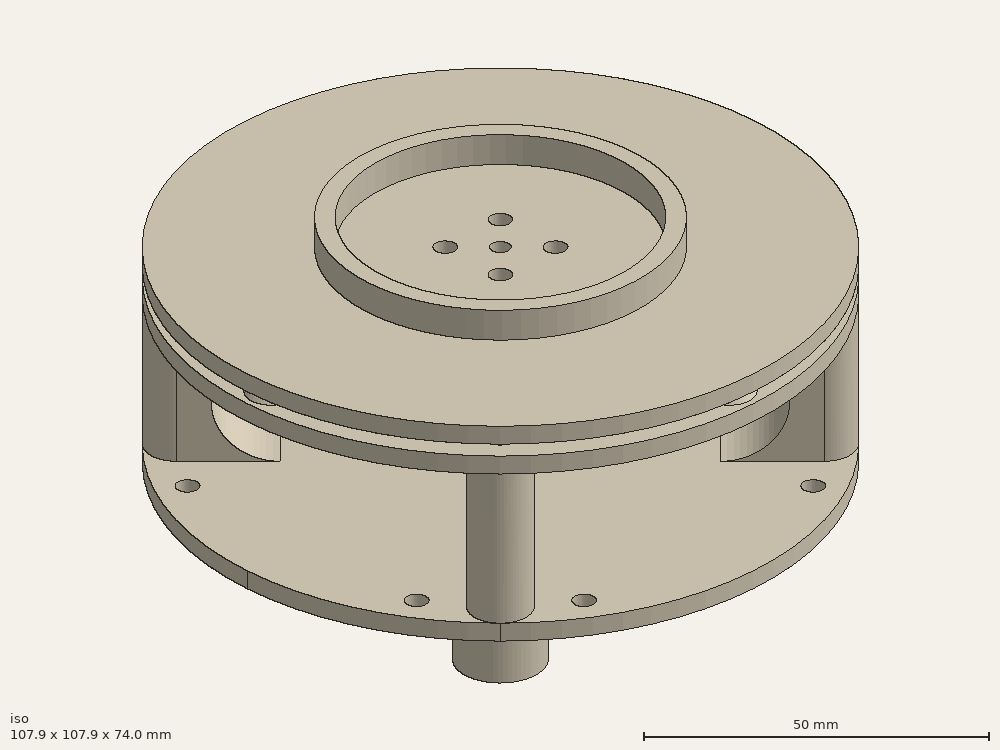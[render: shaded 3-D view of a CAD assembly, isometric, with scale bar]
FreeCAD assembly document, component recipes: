
FREECAD ASSEMBLY — COMPONENT RECIPES ("horiz")

This assembly document has 7 components, labeled P0..P6 below (a component is one placed body or linked part). 7 of them carry a construction recipe — the FreeCAD feature program that regenerates the part from scratch, quoted from this document or its linked companion documents; the rest are supplied as boundary geometry only. No exploded tour is included for this assembly.
COMPONENT P0 — recipe-attached ("Wheel", modeled in this document).
Construction recipe (the document's own serialized feature program — sketch geometry with constraints, then the solid features built on it; lengths are millimeters unless a unit is written):

FEATURE [Sketcher::SketchObject] Sketch001
  ArcFitTolerance = 1e-06
  AttachmentSupport = -> [XY_Plane]
  FullyConstrained = true
  MakeInternals = false
  MapMode = 5
  sketch-geometry (2):
    g0: Circle CenterX=0 CenterY=0 CenterZ=0 NormalX=0 NormalY=0 NormalZ=1 AngleXU=0 Radius=52
    g1: Circle CenterX=0 CenterY=0 CenterZ=0 NormalX=0 NormalY=0 NormalZ=1 AngleXU=0 Radius=1.6
  constraints (4):
    c: Coincident(g0,g-1)
    c: Radius(g0) = 52
    c: Coincident(g1,g0)
    c: Radius(g1) = 1.6
FEATURE [PartDesign::Pad] Pad001
  Direction = (0,0,1)
  Length = 3
  Length2 = 10
  Profile = -> Sketch001
  ReferenceAxis = -> Sketch001 [N_Axis]
  Reversed = true
  Suppressed = false
  Type = 0
FEATURE [Sketcher::SketchObject] Sketch
  ArcFitTolerance = 1e-06
  AttachmentSupport = -> [XY_Plane]
  FullyConstrained = true
  MakeInternals = false
  MapMode = 5
  sketch-geometry (2):
    g0: Circle CenterX=0 CenterY=0 CenterZ=0 NormalX=0 NormalY=0 NormalZ=1 AngleXU=0 Radius=24
    g1: Circle CenterX=0 CenterY=0 CenterZ=0 NormalX=0 NormalY=0 NormalZ=1 AngleXU=0 Radius=27
  constraints (4):
    c: Coincident(g0,g-1)
    c: Coincident(g1,g0)
    c: Radius(g1) = 27
    c: Radius(g0) = 24
FEATURE [PartDesign::Pad] Pad
  BaseFeature = -> Pad001
  Direction = (0,0,1)
  Length = 5
  Length2 = 10
  Profile = -> Sketch
  ReferenceAxis = -> Sketch [N_Axis]
  Suppressed = false
  Type = 0
FEATURE [Sketcher::SketchObject] Sketch002
  ArcFitTolerance = 1e-06
  AttachmentSupport = -> [XY_Plane]
  FullyConstrained = true
  MakeInternals = false
  MapMode = 5
  sketch-geometry (9):
    g0: LineSegment [constr] StartX=-5.65685 StartY=5.65685 StartZ=0 EndX=-5.65685 EndY=-5.65685 EndZ=0
    g1: LineSegment [constr] StartX=-5.65685 StartY=-5.65685 StartZ=0 EndX=5.65685 EndY=-5.65685 EndZ=0
    g2: LineSegment [constr] StartX=5.65685 StartY=-5.65685 StartZ=0 EndX=5.65685 EndY=5.65685 EndZ=0
    g3: LineSegment [constr] StartX=5.65685 StartY=5.65685 StartZ=0 EndX=-5.65685 EndY=5.65685 EndZ=0
    g4: Circle [constr] CenterX=0 CenterY=0 CenterZ=0 NormalX=0 NormalY=0 NormalZ=1 AngleXU=0 Radius=8
    g5: Circle CenterX=5.65685 CenterY=5.65685 CenterZ=0 NormalX=0 NormalY=0 NormalZ=1 AngleXU=0 Radius=1.8
    g6: Circle CenterX=-5.65685 CenterY=5.65685 CenterZ=0 NormalX=0 NormalY=0 NormalZ=1 AngleXU=0 Radius=1.8
    g7: Circle CenterX=-5.65685 CenterY=-5.65685 CenterZ=0 NormalX=0 NormalY=0 NormalZ=1 AngleXU=0 Radius=1.8
    g8: Circle CenterX=5.65685 CenterY=-5.65685 CenterZ=0 NormalX=0 NormalY=0 NormalZ=1 AngleXU=0 Radius=1.8
  constraints (22):
    c: Coincident(g0,g1)
    c: Coincident(g1,g2)
    c: Coincident(g2,g3)
    c: Coincident(g3,g0)
    c: Equal(g0,g1)
    c: Equal(g0,g2)
    c: Equal(g0,g3)
    c: PointOnObject(g0,g4)
    c: PointOnObject(g1,g4)
    c: PointOnObject(g2,g4)
    c: PointOnObject(g3,g4)
    c: Coincident(g4,g-1)
    c: Radius(g4) = 8
    c: Parallel(g3,g-1)
    c: Coincident(g5,g2)
    c: Coincident(g6,g0)
    c: Coincident(g7,g0)
    c: Coincident(g8,g1)
    c: Equal(g8,g5)
    c: Equal(g5,g6)
    c: Equal(g6,g7)
    c: Radius(g5) = 1.8
FEATURE [PartDesign::Pocket] Pocket
  BaseFeature = -> Pad
  Direction = (0,0,-1)
  Length = 5
  Length2 = 5
  Profile = -> Sketch002
  ReferenceAxis = -> Sketch002 [N_Axis]
  Suppressed = false
  Type = 0
FEATURE [PartDesign::Body] Body  label="Wheel"
  AllowCompound = false
  Group = -> [Pad001,Sketch001,Sketch,Pad,Sketch002,Pocket]
  Origin = -> Origin
  Placement = pos=(-1.14e-14,-1.2e-14,59) rot=(0,0,-1;3.14159rad)
  Tip = -> Pocket
COMPONENT P1 — recipe-attached ("Mid", modeled in this document).
Construction recipe (the document's own serialized feature program — sketch geometry with constraints, then the solid features built on it; lengths are millimeters unless a unit is written):

FEATURE [Sketcher::SketchObject] Sketch003
  ArcFitTolerance = 1e-06
  AttachmentSupport = -> [XY_Plane001]
  FullyConstrained = true
  MakeInternals = false
  MapMode = 5
  sketch-geometry (11):
    g0: Circle CenterX=0 CenterY=0 CenterZ=0 NormalX=0 NormalY=0 NormalZ=1 AngleXU=0 Radius=52
    g1: Circle CenterX=0 CenterY=0 CenterZ=0 NormalX=0 NormalY=0 NormalZ=1 AngleXU=0 Radius=1.6
    g2: LineSegment [constr] StartX=-8.48528 StartY=8.48528 StartZ=0 EndX=-8.48528 EndY=-8.48528 EndZ=0
    g3: LineSegment [constr] StartX=-8.48528 StartY=-8.48528 StartZ=0 EndX=8.48528 EndY=-8.48528 EndZ=0
    g4: LineSegment [constr] StartX=8.48528 StartY=-8.48528 StartZ=0 EndX=8.48528 EndY=8.48528 EndZ=0
    g5: LineSegment [constr] StartX=8.48528 StartY=8.48528 StartZ=0 EndX=-8.48528 EndY=8.48528 EndZ=0
    g6: Circle [constr] CenterX=0 CenterY=0 CenterZ=0 NormalX=0 NormalY=0 NormalZ=1 AngleXU=0 Radius=12
    g7: Circle CenterX=8.48528 CenterY=8.48528 CenterZ=0 NormalX=0 NormalY=0 NormalZ=1 AngleXU=0 Radius=2.2
    g8: Circle CenterX=-8.48528 CenterY=8.48528 CenterZ=0 NormalX=0 NormalY=0 NormalZ=1 AngleXU=0 Radius=2.2
    g9: Circle CenterX=-8.48528 CenterY=-8.48528 CenterZ=0 NormalX=0 NormalY=0 NormalZ=1 AngleXU=0 Radius=2.2
    g10: Circle CenterX=8.48528 CenterY=-8.48528 CenterZ=0 NormalX=0 NormalY=0 NormalZ=1 AngleXU=0 Radius=2.2
  constraints (26):
    c: Coincident(g0,g-1)
    c: Radius(g0) = 52
    c: Coincident(g1,g0)
    c: Radius(g1) = 1.6
    c: Coincident(g2,g3)
    c: Coincident(g3,g4)
    c: Coincident(g4,g5)
    c: Coincident(g5,g2)
    c: Equal(g2,g3)
    c: Equal(g2,g4)
    c: Equal(g2,g5)
    c: PointOnObject(g2,g6)
    c: PointOnObject(g3,g6)
    c: PointOnObject(g4,g6)
    c: PointOnObject(g5,g6)
    c: Coincident(g6,g0)
    c: Radius(g6) = 12
    c: Parallel(g5,g-1)
    c: Coincident(g7,g4)
    c: Coincident(g8,g2)
    c: Coincident(g9,g2)
    c: Coincident(g10,g3)
    c: Equal(g10,g7)
    c: Equal(g7,g8)
    c: Equal(g8,g9)
    c: Radius(g7) = 2.2
FEATURE [PartDesign::Pad] Pad002
  Direction = (0,0,1)
  Length = 3
  Length2 = 10
  Profile = -> Sketch003
  ReferenceAxis = -> Sketch003 [N_Axis]
  Suppressed = false
  Type = 0
FEATURE [Sketcher::SketchObject] Sketch005
  ArcFitTolerance = 1e-06
  AttachmentSupport = -> [XY_Plane001]
  FullyConstrained = true
  MakeInternals = false
  MapMode = 5
  sketch-geometry (9):
    g0: LineSegment [constr] StartX=33.234 StartY=33.234 StartZ=0 EndX=-33.234 EndY=33.234 EndZ=0
    g1: LineSegment [constr] StartX=-33.234 StartY=33.234 StartZ=0 EndX=-33.234 EndY=-33.234 EndZ=0
    g2: LineSegment [constr] StartX=-33.234 StartY=-33.234 StartZ=0 EndX=33.234 EndY=-33.234 EndZ=0
    g3: LineSegment [constr] StartX=33.234 StartY=-33.234 StartZ=0 EndX=33.234 EndY=33.234 EndZ=0
    g4: Circle [constr] CenterX=-2e-16 CenterY=0 CenterZ=0 NormalX=0 NormalY=0 NormalZ=1 AngleXU=0 Radius=47
    g5: Circle CenterX=33.234 CenterY=33.234 CenterZ=0 NormalX=0 NormalY=0 NormalZ=1 AngleXU=0 Radius=5
    g6: Circle CenterX=-33.234 CenterY=33.234 CenterZ=0 NormalX=0 NormalY=0 NormalZ=1 AngleXU=0 Radius=5
    g7: Circle CenterX=-33.234 CenterY=-33.234 CenterZ=0 NormalX=0 NormalY=0 NormalZ=1 AngleXU=0 Radius=5
    g8: Circle CenterX=33.234 CenterY=-33.234 CenterZ=0 NormalX=0 NormalY=0 NormalZ=1 AngleXU=0 Radius=5
  constraints (22):
    c: Coincident(g0,g1)
    c: Coincident(g1,g2)
    c: Coincident(g2,g3)
    c: Coincident(g3,g0)
    c: Equal(g0,g1)
    c: Equal(g0,g2)
    c: Equal(g0,g3)
    c: PointOnObject(g0,g4)
    c: PointOnObject(g1,g4)
    c: PointOnObject(g2,g4)
    c: PointOnObject(g3,g4)
    c: Coincident(g4,g-1)
    c: Radius(g4) = 47
    c: Parallel(g0,g-1)
    c: Coincident(g5,g0)
    c: Coincident(g6,g0)
    c: Coincident(g7,g1)
    c: Coincident(g8,g2)
    c: Equal(g8,g5)
    c: Equal(g5,g6)
    c: Equal(g6,g7)
    c: Radius(g6) = 5
FEATURE [PartDesign::Pad] Pad004
  BaseFeature = -> Pad002
  Direction = (0,0,1)
  Length = 28
  Length2 = 10
  Profile = -> Sketch005
  ReferenceAxis = -> Sketch005 [N_Axis]
  Suppressed = false
  Type = 0
FEATURE [Sketcher::SketchObject] Sketch007
  ArcFitTolerance = 1e-06
  AttachmentOffset = pos=(0,0,28) rot=(0,0,1;0rad)
  AttachmentSupport = -> [XY_Plane001]
  FullyConstrained = true
  MakeInternals = false
  MapMode = 5
  Placement = pos=(0,0,28) rot=(0,0,1;0rad)
  sketch-geometry (9):
    g0: LineSegment [constr] StartX=-33.234 StartY=33.234 StartZ=0 EndX=-33.234 EndY=-33.234 EndZ=0
    g1: LineSegment [constr] StartX=-33.234 StartY=-33.234 StartZ=0 EndX=33.234 EndY=-33.234 EndZ=0
    g2: LineSegment [constr] StartX=33.234 StartY=-33.234 StartZ=0 EndX=33.234 EndY=33.234 EndZ=0
    g3: LineSegment [constr] StartX=33.234 StartY=33.234 StartZ=0 EndX=-33.234 EndY=33.234 EndZ=0
    g4: Circle [constr] CenterX=0 CenterY=0 CenterZ=0 NormalX=0 NormalY=0 NormalZ=1 AngleXU=0 Radius=47
    g5: Circle CenterX=33.234 CenterY=33.234 CenterZ=0 NormalX=0 NormalY=0 NormalZ=1 AngleXU=0 Radius=1.5
    g6: Circle CenterX=-33.234 CenterY=33.234 CenterZ=0 NormalX=0 NormalY=0 NormalZ=1 AngleXU=0 Radius=1.5
    g7: Circle CenterX=-33.234 CenterY=-33.234 CenterZ=0 NormalX=0 NormalY=0 NormalZ=1 AngleXU=0 Radius=1.5
    g8: Circle CenterX=33.234 CenterY=-33.234 CenterZ=0 NormalX=0 NormalY=0 NormalZ=1 AngleXU=0 Radius=1.5
  constraints (22):
    c: Coincident(g0,g1)
    c: Coincident(g1,g2)
    c: Coincident(g2,g3)
    c: Coincident(g3,g0)
    c: Equal(g0,g1)
    c: Equal(g0,g2)
    c: Equal(g0,g3)
    c: PointOnObject(g0,g4)
    c: PointOnObject(g1,g4)
    c: PointOnObject(g2,g4)
    c: PointOnObject(g3,g4)
    c: Coincident(g4,g-1)
    c: Radius(g4) = 47
    c: Parallel(g3,g-1)
    c: Coincident(g5,g2)
    c: Coincident(g6,g0)
    c: Coincident(g7,g0)
    c: Coincident(g8,g1)
    c: Equal(g8,g5)
    c: Equal(g5,g6)
    c: Equal(g6,g7)
    c: Radius(g6) = 1.5
FEATURE [PartDesign::Pocket] Pocket002
  BaseFeature = -> Pad004
  Direction = (0,0,-1)
  Length = 10
  Length2 = 5
  Profile = -> Sketch007
  ReferenceAxis = -> Sketch007 [N_Axis]
  Suppressed = false
  Type = 0
FEATURE [Sketcher::SketchObject] Sketch011
  ArcFitTolerance = 1e-06
  AttachmentSupport = -> [XY_Plane001]
  FullyConstrained = true
  MakeInternals = false
  MapMode = 5
  sketch-geometry (17):
    g0: LineSegment [constr] StartX=-23.5 StartY=-40.7032 StartZ=0 EndX=40.7032 EndY=-23.5 EndZ=0
    g1: LineSegment [constr] StartX=40.7032 StartY=-23.5 StartZ=0 EndX=23.5 EndY=40.7032 EndZ=0
    g2: LineSegment [constr] StartX=23.5 StartY=40.7032 StartZ=0 EndX=-40.7032 EndY=23.5 EndZ=0
    g3: LineSegment [constr] StartX=-40.7032 StartY=23.5 StartZ=0 EndX=-23.5 EndY=-40.7032 EndZ=0
    g4: Circle [constr] CenterX=0 CenterY=0 CenterZ=0 NormalX=0 NormalY=0 NormalZ=1 AngleXU=0 Radius=47
    g5: Circle CenterX=23.5 CenterY=40.7032 CenterZ=0 NormalX=0 NormalY=0 NormalZ=1 AngleXU=0 Radius=1.8
    g6: Circle CenterX=-40.7032 CenterY=23.5 CenterZ=0 NormalX=0 NormalY=0 NormalZ=1 AngleXU=0 Radius=1.8
    g7: Circle CenterX=-23.5 CenterY=-40.7032 CenterZ=0 NormalX=0 NormalY=0 NormalZ=1 AngleXU=0 Radius=1.8
    g8: Circle CenterX=40.7032 CenterY=-23.5 CenterZ=0 NormalX=0 NormalY=0 NormalZ=1 AngleXU=0 Radius=1.8
    g9: LineSegment [constr] StartX=-23.5 StartY=40.7032 StartZ=0 EndX=40.7032 EndY=23.5 EndZ=0
    g10: LineSegment [constr] StartX=40.7032 StartY=23.5 StartZ=0 EndX=23.5 EndY=-40.7032 EndZ=0
    g11: LineSegment [constr] StartX=23.5 StartY=-40.7032 StartZ=0 EndX=-40.7032 EndY=-23.5 EndZ=0
    g12: LineSegment [constr] StartX=-40.7032 StartY=-23.5 StartZ=0 EndX=-23.5 EndY=40.7032 EndZ=0
    g13: Circle CenterX=-23.5 CenterY=40.7032 CenterZ=0 NormalX=0 NormalY=0 NormalZ=1 AngleXU=0 Radius=1.8
    g14: Circle CenterX=40.7032 CenterY=23.5 CenterZ=0 NormalX=0 NormalY=0 NormalZ=1 AngleXU=0 Radius=1.8
    g15: Circle CenterX=23.5 CenterY=-40.7032 CenterZ=0 NormalX=0 NormalY=0 NormalZ=1 AngleXU=0 Radius=1.8
    g16: Circle CenterX=-40.7032 CenterY=-23.5 CenterZ=0 NormalX=0 NormalY=0 NormalZ=1 AngleXU=0 Radius=1.8
  constraints (42):
    c: Coincident(g0,g1)
    c: Coincident(g1,g2)
    c: Coincident(g2,g3)
    c: Coincident(g3,g0)
    c: Equal(g0,g1)
    c: Equal(g0,g2)
    c: Equal(g0,g3)
    c: PointOnObject(g0,g4)
    c: PointOnObject(g1,g4)
    c: PointOnObject(g2,g4)
    c: PointOnObject(g3,g4)
    c: Coincident(g4,g-1)
    c: Radius(g4) = 47
    c: Coincident(g5,g1)
    c: Coincident(g6,g2)
    c: Coincident(g7,g0)
    c: Coincident(g8,g0)
    c: Equal(g8,g7)
    c: Equal(g7,g6)
    c: Equal(g6,g5)
    c: Radius(g5) = 1.8
    c: Angle(g-1,g0) = 0.261799
    c: PointOnObject(g9,g4)
    c: PointOnObject(g9,g4)
    c: Coincident(g9,g10)
    c: PointOnObject(g10,g4)
    c: Coincident(g10,g11)
    c: PointOnObject(g11,g4)
    c: Coincident(g11,g12)
    c: Coincident(g12,g9)
    c: Equal(g9,g10)
    c: Angle(g11,g12) = 1.5708
    c: Angle(g10,g11) = 1.5708
    c: Angle(g10,g-2) = 0.261799
    c: Coincident(g13,g9)
    c: Coincident(g14,g9)
    c: Coincident(g15,g10)
    c: Coincident(g16,g11)
    c: Equal(g16,g15)
    c: Equal(g15,g14)
    c: Equal(g14,g13)
    c: Equal(g13,g5)
FEATURE [PartDesign::Pocket] Pocket004
  BaseFeature = -> Pocket002
  Direction = (0,0,-1)
  Length = 5
  Length2 = 5
  Profile = -> Sketch011
  ReferenceAxis = -> Sketch011 [N_Axis]
  Reversed = true
  Suppressed = false
  Type = 0
FEATURE [Sketcher::SketchObject] Sketch018
  ArcFitTolerance = 1e-06
  AttachmentOffset = pos=(0,0,0) rot=(0,1,0;0.785398rad)
  AttachmentSupport = -> [YZ_Plane001]
  FullyConstrained = true
  MakeInternals = false
  MapMode = 5
  Placement = pos=(0,0,0) rot=(0.281085,0.678598,0.678598;2.59356rad)
  sketch-geometry (10):
    g0: LineSegment StartX=-47 StartY=18 StartZ=0 EndX=-47 EndY=3 EndZ=0
    g1: LineSegment StartX=-47 StartY=3 StartZ=0 EndX=-32 EndY=3 EndZ=0
    g2: LineSegment StartX=-42 StartY=13 StartZ=0 EndX=-42 EndY=18 EndZ=0
    g3: LineSegment StartX=-42 StartY=18 StartZ=0 EndX=-47 EndY=18 EndZ=0
    g4: ArcOfCircle CenterX=-32 CenterY=13 CenterZ=0 NormalX=0 NormalY=0 NormalZ=1 AngleXU=0 Radius=10 StartAngle=3.14159 EndAngle=4.71239
    g5: LineSegment StartX=47 StartY=18 StartZ=0 EndX=47 EndY=3 EndZ=0
    g6: LineSegment StartX=47 StartY=3 StartZ=0 EndX=32 EndY=3 EndZ=0
    g7: LineSegment StartX=42 StartY=13 StartZ=0 EndX=42 EndY=18 EndZ=0
    g8: LineSegment StartX=42 StartY=18 StartZ=0 EndX=47 EndY=18 EndZ=0
    g9: ArcOfCircle CenterX=32 CenterY=13 CenterZ=0 NormalX=0 NormalY=0 NormalZ=1 AngleXU=0 Radius=10 StartAngle=4.71239 EndAngle=6.28319
  constraints (27):
    c: Coincident(g0,g1)
    c: Coincident(g2,g3)
    c: Coincident(g3,g0)
    c: Vertical(g0)
    c: Vertical(g2)
    c: Horizontal(g1)
    c: Horizontal(g3)
    c: Coincident(g4,g2)
    c: Coincident(g4,g1)
    c: DistanceX(g1,g4) = 0
    c: DistanceY(g0) = 3
    c: DistanceX(g0,g-1) = 47
    c: DistanceX(g3,g3) = 5
    c: DistanceY(g0,g0) = 15
    c: DistanceY(g2,g4) = 0
    c: Radius(g4) = 10
    c: Symmetric(g0,g5,g-2)
    c: Symmetric(g0,g5,g-2)
    c: Symmetric(g1,g6,g-2)
    c: Symmetric(g1,g6,g-2)
    c: Symmetric(g2,g7,g-2)
    c: Symmetric(g2,g7,g-2)
    c: Symmetric(g3,g8,g-2)
    c: Symmetric(g3,g8,g-2)
    c: Equal(g4,g9)
    c: Symmetric(g4,g9,g-2)
    c: Symmetric(g4,g9,g-2)
FEATURE [PartDesign::Pad] Pad011
  BaseFeature = -> Pocket004
  Direction = (0.707107,0.707107,0)
  Length = 10
  Length2 = 10
  Midplane = true
  Profile = -> Sketch018
  ReferenceAxis = -> Sketch018 [N_Axis]
  Suppressed = false
  Type = 0
FEATURE [Sketcher::SketchObject] Sketch019
  ArcFitTolerance = 1e-06
  AttachmentOffset = pos=(0,0,0) rot=(0,1,0;-0.785398rad)
  AttachmentSupport = -> [YZ_Plane001]
  FullyConstrained = true
  MakeInternals = false
  MapMode = 5
  Placement = pos=(0,0,0) rot=(-0.862856,-0.357407,-0.357407;4.56541rad)
  sketch-geometry (10):
    g0: LineSegment StartX=-47 StartY=18 StartZ=0 EndX=-47 EndY=3 EndZ=0
    g1: LineSegment StartX=-47 StartY=3 StartZ=0 EndX=-32 EndY=3 EndZ=0
    g2: LineSegment StartX=-42 StartY=13 StartZ=0 EndX=-42 EndY=18 EndZ=0
    g3: LineSegment StartX=-42 StartY=18 StartZ=0 EndX=-47 EndY=18 EndZ=0
    g4: ArcOfCircle CenterX=-32 CenterY=13 CenterZ=0 NormalX=0 NormalY=0 NormalZ=1 AngleXU=0 Radius=10 StartAngle=3.14159 EndAngle=4.71239
    g5: LineSegment StartX=47 StartY=18 StartZ=0 EndX=47 EndY=3 EndZ=0
    g6: LineSegment StartX=47 StartY=3 StartZ=0 EndX=32 EndY=3 EndZ=0
    g7: LineSegment StartX=42 StartY=13 StartZ=0 EndX=42 EndY=18 EndZ=0
    g8: LineSegment StartX=42 StartY=18 StartZ=0 EndX=47 EndY=18 EndZ=0
    g9: ArcOfCircle CenterX=32 CenterY=13 CenterZ=0 NormalX=0 NormalY=0 NormalZ=1 AngleXU=0 Radius=10 StartAngle=4.71239 EndAngle=6.28319
  constraints (27):
    c: Coincident(g0,g1)
    c: Coincident(g2,g3)
    c: Coincident(g3,g0)
    c: Vertical(g0)
    c: Vertical(g2)
    c: Horizontal(g1)
    c: Horizontal(g3)
    c: Coincident(g4,g2)
    c: Coincident(g4,g1)
    c: DistanceX(g1,g4) = 0
    c: DistanceY(g0) = 3
    c: DistanceX(g0,g-1) = 47
    c: DistanceX(g3,g3) = 5
    c: DistanceY(g0,g0) = 15
    c: DistanceY(g2,g4) = 0
    c: Radius(g4) = 10
    c: Symmetric(g0,g5,g-2)
    c: Symmetric(g0,g5,g-2)
    c: Symmetric(g1,g6,g-2)
    c: Symmetric(g1,g6,g-2)
    c: Symmetric(g2,g7,g-2)
    c: Symmetric(g2,g7,g-2)
    c: Symmetric(g3,g8,g-2)
    c: Symmetric(g3,g8,g-2)
    c: Equal(g4,g9)
    c: Symmetric(g4,g9,g-2)
    c: Symmetric(g4,g9,g-2)
FEATURE [PartDesign::Pad] Pad012
  BaseFeature = -> Pad011
  Direction = (0.707107,-0.707107,0)
  Length = 10
  Length2 = 10
  Midplane = true
  Profile = -> Sketch019
  ReferenceAxis = -> Sketch019 [N_Axis]
  Suppressed = false
  Type = 0
FEATURE [PartDesign::Body] Body001  label="Mid"
  AllowCompound = false
  Group = -> [Sketch003,Pad002,Sketch005,Pad004,Sketch007,Pocket002,Sketch011,Pocket004,Sketch018,Pad011,Sketch019,Pad012]
  Origin = -> Origin001
  Placement = pos=(-2.8e-15,-2.2e-15,23) rot=(0,0,-1;3.14159rad)
  Tip = -> Pad012
COMPONENT P2 — recipe-attached ("Top", modeled in this document).
Construction recipe (the document's own serialized feature program — sketch geometry with constraints, then the solid features built on it; lengths are millimeters unless a unit is written):

FEATURE [Sketcher::SketchObject] Sketch004
  ArcFitTolerance = 1e-06
  AttachmentSupport = -> [XY_Plane002]
  FullyConstrained = true
  MakeInternals = false
  MapMode = 5
  sketch-geometry (11):
    g0: Circle CenterX=0 CenterY=0 CenterZ=0 NormalX=0 NormalY=0 NormalZ=1 AngleXU=0 Radius=52
    g1: Circle CenterX=0 CenterY=0 CenterZ=0 NormalX=0 NormalY=0 NormalZ=1 AngleXU=0 Radius=1.6
    g2: LineSegment [constr] StartX=-8.48528 StartY=8.48528 StartZ=0 EndX=-8.48528 EndY=-8.48528 EndZ=0
    g3: LineSegment [constr] StartX=-8.48528 StartY=-8.48528 StartZ=0 EndX=8.48528 EndY=-8.48528 EndZ=0
    g4: LineSegment [constr] StartX=8.48528 StartY=-8.48528 StartZ=0 EndX=8.48528 EndY=8.48528 EndZ=0
    g5: LineSegment [constr] StartX=8.48528 StartY=8.48528 StartZ=0 EndX=-8.48528 EndY=8.48528 EndZ=0
    g6: Circle [constr] CenterX=0 CenterY=0 CenterZ=0 NormalX=0 NormalY=0 NormalZ=1 AngleXU=0 Radius=12
    g7: Circle CenterX=8.48528 CenterY=8.48528 CenterZ=0 NormalX=0 NormalY=0 NormalZ=1 AngleXU=0 Radius=2.2
    g8: Circle CenterX=-8.48528 CenterY=8.48528 CenterZ=0 NormalX=0 NormalY=0 NormalZ=1 AngleXU=0 Radius=2.2
    g9: Circle CenterX=-8.48528 CenterY=-8.48528 CenterZ=0 NormalX=0 NormalY=0 NormalZ=1 AngleXU=0 Radius=2.2
    g10: Circle CenterX=8.48528 CenterY=-8.48528 CenterZ=0 NormalX=0 NormalY=0 NormalZ=1 AngleXU=0 Radius=2.2
  constraints (26):
    c: Coincident(g0,g-1)
    c: Radius(g0) = 52
    c: Coincident(g1,g0)
    c: Radius(g1) = 1.6
    c: Coincident(g2,g3)
    c: Coincident(g3,g4)
    c: Coincident(g4,g5)
    c: Coincident(g5,g2)
    c: Equal(g2,g3)
    c: Equal(g2,g4)
    c: Equal(g2,g5)
    c: PointOnObject(g2,g6)
    c: PointOnObject(g3,g6)
    c: PointOnObject(g4,g6)
    c: PointOnObject(g5,g6)
    c: Coincident(g6,g0)
    c: Radius(g6) = 12
    c: Parallel(g5,g-1)
    c: Coincident(g7,g4)
    c: Coincident(g8,g2)
    c: Coincident(g9,g2)
    c: Coincident(g10,g3)
    c: Equal(g10,g7)
    c: Equal(g7,g8)
    c: Equal(g8,g9)
    c: Radius(g7) = 2.2
FEATURE [PartDesign::Pad] Pad003
  Direction = (0,0,1)
  Length = 3
  Length2 = 10
  Profile = -> Sketch004
  ReferenceAxis = -> Sketch004 [N_Axis]
  Suppressed = false
  Type = 0
FEATURE [Sketcher::SketchObject] Sketch006
  ArcFitTolerance = 1e-06
  AttachmentSupport = -> [XY_Plane002]
  FullyConstrained = true
  MakeInternals = false
  MapMode = 5
  sketch-geometry (9):
    g0: LineSegment [constr] StartX=33.234 StartY=-33.234 StartZ=0 EndX=33.234 EndY=33.234 EndZ=0
    g1: LineSegment [constr] StartX=33.234 StartY=33.234 StartZ=0 EndX=-33.234 EndY=33.234 EndZ=0
    g2: LineSegment [constr] StartX=-33.234 StartY=33.234 StartZ=0 EndX=-33.234 EndY=-33.234 EndZ=0
    g3: LineSegment [constr] StartX=-33.234 StartY=-33.234 StartZ=0 EndX=33.234 EndY=-33.234 EndZ=0
    g4: Circle [constr] CenterX=0 CenterY=0 CenterZ=0 NormalX=0 NormalY=0 NormalZ=1 AngleXU=0 Radius=47
    g5: Circle CenterX=-33.234 CenterY=33.234 CenterZ=0 NormalX=0 NormalY=0 NormalZ=1 AngleXU=0 Radius=1.8
    g6: Circle CenterX=-33.234 CenterY=-33.234 CenterZ=0 NormalX=0 NormalY=0 NormalZ=1 AngleXU=0 Radius=1.8
    g7: Circle CenterX=33.234 CenterY=-33.234 CenterZ=0 NormalX=0 NormalY=0 NormalZ=1 AngleXU=0 Radius=1.8
    g8: Circle CenterX=33.234 CenterY=33.234 CenterZ=0 NormalX=0 NormalY=0 NormalZ=1 AngleXU=0 Radius=1.8
  constraints (22):
    c: Coincident(g0,g1)
    c: Coincident(g1,g2)
    c: Coincident(g2,g3)
    c: Coincident(g3,g0)
    c: Equal(g0,g1)
    c: Equal(g0,g2)
    c: Equal(g0,g3)
    c: PointOnObject(g0,g4)
    c: PointOnObject(g1,g4)
    c: PointOnObject(g2,g4)
    c: PointOnObject(g3,g4)
    c: Coincident(g4,g-1)
    c: Radius(g4) = 47
    c: Parallel(g1,g-1)
    c: Coincident(g5,g1)
    c: Coincident(g6,g2)
    c: Coincident(g7,g0)
    c: Coincident(g8,g0)
    c: Equal(g8,g7)
    c: Equal(g7,g6)
    c: Equal(g6,g5)
    c: Radius(g5) = 1.8
FEATURE [PartDesign::Pocket] Pocket001
  BaseFeature = -> Pad003
  Direction = (0,0,-1)
  Length = 5
  Length2 = 5
  Midplane = true
  Profile = -> Sketch006
  ReferenceAxis = -> Sketch006 [N_Axis]
  Suppressed = false
  Type = 1
FEATURE [PartDesign::AdditiveSphere] Sphere
  Angle1 = 0
  Angle2 = 90
  Angle3 = 360
  AttacherType = Attacher::AttachEngine3D
  AttachmentOffset = pos=(0,47,0) rot=(0,0,1;0rad)
  AttachmentSupport = -> [XY_Plane002]
  BaseFeature = -> Pocket001
  MapMode = 5
  Placement = pos=(0,47,0) rot=(0,0,1;0rad)
  Radius = 5
  Suppressed = false
FEATURE [PartDesign::AdditiveSphere] Sphere001
  Angle1 = 0
  Angle2 = 90
  Angle3 = 360
  AttacherType = Attacher::AttachEngine3D
  AttachmentOffset = pos=(0,-47,0) rot=(0,0,1;0rad)
  AttachmentSupport = -> [XY_Plane002]
  BaseFeature = -> Sphere
  MapMode = 5
  Placement = pos=(0,-47,0) rot=(0,0,1;0rad)
  Radius = 5
  Suppressed = false
FEATURE [PartDesign::AdditiveSphere] Sphere002
  Angle1 = 0
  Angle2 = 90
  Angle3 = 360
  AttacherType = Attacher::AttachEngine3D
  AttachmentOffset = pos=(47,0,0) rot=(0,0,1;0rad)
  AttachmentSupport = -> [XY_Plane002]
  BaseFeature = -> Sphere001
  MapMode = 5
  Placement = pos=(47,0,0) rot=(0,0,1;0rad)
  Radius = 5
  Suppressed = false
FEATURE [PartDesign::AdditiveSphere] Sphere003
  Angle1 = 0
  Angle2 = 90
  Angle3 = 360
  AttacherType = Attacher::AttachEngine3D
  AttachmentOffset = pos=(-47,0,0) rot=(0,0,1;0rad)
  AttachmentSupport = -> [XY_Plane002]
  BaseFeature = -> Sphere002
  MapMode = 5
  Placement = pos=(-47,0,0) rot=(0,0,1;0rad)
  Radius = 5
  Suppressed = false
FEATURE [PartDesign::Body] Body002  label="Top"
  AllowCompound = false
  Group = -> [Sketch004,Pad003,Sketch006,Pocket001,Sphere,Sphere001,Sphere002,Sphere003]
  Origin = -> Origin002
  Placement = pos=(-6.2e-15,-9.9e-15,51) rot=(0,0,-1;3.14159rad)
  Tip = -> Sphere003
COMPONENT P3 — recipe-attached ("Center", modeled in this document).
Construction recipe (the document's own serialized feature program — sketch geometry with constraints, then the solid features built on it; lengths are millimeters unless a unit is written):

FEATURE [Sketcher::SketchObject] Sketch012
  ArcFitTolerance = 1e-06
  AttachmentSupport = -> [XY_Plane003]
  FullyConstrained = true
  MakeInternals = false
  MapMode = 5
  sketch-geometry (10):
    g0: Circle CenterX=0 CenterY=0 CenterZ=0 NormalX=0 NormalY=0 NormalZ=1 AngleXU=0 Radius=20
    g1: LineSegment [constr] StartX=-8.48528 StartY=8.48528 StartZ=0 EndX=-8.48528 EndY=-8.48528 EndZ=0
    g2: LineSegment [constr] StartX=-8.48528 StartY=-8.48528 StartZ=0 EndX=8.48528 EndY=-8.48528 EndZ=0
    g3: LineSegment [constr] StartX=8.48528 StartY=-8.48528 StartZ=0 EndX=8.48528 EndY=8.48528 EndZ=0
    g4: LineSegment [constr] StartX=8.48528 StartY=8.48528 StartZ=0 EndX=-8.48528 EndY=8.48528 EndZ=0
    g5: Circle [constr] CenterX=0 CenterY=0 CenterZ=0 NormalX=0 NormalY=0 NormalZ=1 AngleXU=0 Radius=12
    g6: Circle CenterX=-8.48528 CenterY=8.48528 CenterZ=0 NormalX=0 NormalY=0 NormalZ=1 AngleXU=0 Radius=2.2
    g7: Circle CenterX=8.48528 CenterY=8.48528 CenterZ=0 NormalX=0 NormalY=0 NormalZ=1 AngleXU=0 Radius=2.2
    g8: Circle CenterX=8.48528 CenterY=-8.48528 CenterZ=0 NormalX=0 NormalY=0 NormalZ=1 AngleXU=0 Radius=2.2
    g9: Circle CenterX=-8.48528 CenterY=-8.48528 CenterZ=0 NormalX=0 NormalY=0 NormalZ=1 AngleXU=0 Radius=2.2
  constraints (25):
    c: Radius(g0) = 20
    c: DistanceX(g0) = 0
    c: DistanceY(g0) = 0
    c: Coincident(g1,g2)
    c: Coincident(g2,g3)
    c: Coincident(g3,g4)
    c: Coincident(g4,g1)
    c: Equal(g1,g2)
    c: Equal(g1,g3)
    c: Equal(g1,g4)
    c: PointOnObject(g1,g5)
    c: PointOnObject(g2,g5)
    c: PointOnObject(g3,g5)
    c: PointOnObject(g4,g5)
    c: Coincident(g5,g0)
    c: Radius(g5) = 12
    c: Parallel(g4,g-1)
    c: Coincident(g6,g1)
    c: Coincident(g7,g3)
    c: Coincident(g8,g2)
    c: Coincident(g9,g1)
    c: Equal(g6,g7)
    c: Equal(g7,g8)
    c: Equal(g8,g9)
    c: Radius(g7) = 2.2
FEATURE [PartDesign::Pad] Pad005
  Direction = (0,0,1)
  Length = 3
  Length2 = 10
  Profile = -> Sketch012
  ReferenceAxis = -> Sketch012 [N_Axis]
  Suppressed = false
  Type = 0
FEATURE [Sketcher::SketchObject] Sketch013
  ArcFitTolerance = 1e-06
  AttachmentSupport = -> [XY_Plane003]
  FullyConstrained = true
  MakeInternals = false
  MapMode = 5
  sketch-geometry (2):
    g0: Circle CenterX=0 CenterY=0 CenterZ=0 NormalX=0 NormalY=0 NormalZ=1 AngleXU=0 Radius=7
    g1: Circle CenterX=0 CenterY=0 CenterZ=0 NormalX=0 NormalY=0 NormalZ=1 AngleXU=0 Radius=3
  constraints (4):
    c: Coincident(g0,g-1)
    c: Radius(g0) = 7
    c: Coincident(g1,g0)
    c: Radius(g1) = 3
FEATURE [PartDesign::Pad] Pad006
  BaseFeature = -> Pad005
  Direction = (0,0,1)
  Length = 30
  Length2 = 10
  Profile = -> Sketch013
  ReferenceAxis = -> Sketch013 [N_Axis]
  Reversed = true
  Suppressed = false
  Type = 0
FEATURE [PartDesign::Body] Body003  label="Center"
  AllowCompound = false
  Group = -> [Sketch012,Pad005,Sketch013,Pad006]
  Origin = -> Origin003
  Placement = pos=(0,0,20) rot=(0,0,1;0rad)
  Tip = -> Pad006
COMPONENT P4 — recipe-attached ("Leg2", modeled in this document).
Construction recipe (the document's own serialized feature program — sketch geometry with constraints, then the solid features built on it; lengths are millimeters unless a unit is written):

FEATURE [Sketcher::SketchObject] Sketch014
  ArcFitTolerance = 1e-06
  AttachmentSupport = -> [XY_Plane004]
  FullyConstrained = true
  MakeInternals = false
  MapMode = 5
  sketch-geometry (9):
    g0: ArcOfCircle CenterX=0 CenterY=-1.8e-15 CenterZ=0 NormalX=0 NormalY=0 NormalZ=1 AngleXU=0 Radius=52 StartAngle=5.95835 EndAngle=6.60802
    g1: ArcOfCircle CenterX=0 CenterY=-1.8e-15 CenterZ=0 NormalX=0 NormalY=0 NormalZ=1 AngleXU=0 Radius=42 StartAngle=5.95835 EndAngle=6.60802
    g2: ArcOfCircle CenterX=44.5421 CenterY=15 CenterZ=0 NormalX=0 NormalY=0 NormalZ=1 AngleXU=0 Radius=5 StartAngle=0.324831 EndAngle=3.46643
    g3: ArcOfCircle CenterX=44.5421 CenterY=-15 CenterZ=0 NormalX=0 NormalY=0 NormalZ=1 AngleXU=0 Radius=5 StartAngle=2.81676 EndAngle=5.95836
    g4: LineSegment [constr] StartX=52 StartY=0 StartZ=0 EndX=0 EndY=-1.8e-15 EndZ=0
    g5: LineSegment [constr] StartX=45.3985 StartY=12.1645 StartZ=0 EndX=0 EndY=-1.8e-15 EndZ=0
    g6: LineSegment [constr] StartX=0 StartY=-1.8e-15 StartZ=0 EndX=45.3985 EndY=-12.1645 EndZ=0
    g7: Circle CenterX=45.3985 CenterY=12.1645 CenterZ=0 NormalX=0 NormalY=0 NormalZ=1 AngleXU=0 Radius=1.5
    g8: Circle CenterX=45.3985 CenterY=-12.1645 CenterZ=0 NormalX=0 NormalY=0 NormalZ=1 AngleXU=0 Radius=1.5
  constraints (24):
    c: Coincident(g0,g-1)
    c: Coincident(g1,g0)
    c: Radius(g0) = 52
    c: Radius(g1) = 42
    c: Tangent(g2,g0) = -1.5708
    c: Tangent(g3,g1) = 1.5708
    c: PointOnObject(g4,g0)
    c: Coincident(g4,g0)
    c: Angle(g-1,g4) = 0
    c: Symmetric(g2,g3,g4)
    c: Distance(g3,g2) = 30
    c: Coincident(g2,g1)
    c: Coincident(g3,g0)
    c: Radius(g2) = 5
    c: Coincident(g5,g0)
    c: Coincident(g6,g0)
    c: Distance(g5) = 47
    c: Distance(g6) = 47
    c: Coincident(g7,g5)
    c: Coincident(g8,g6)
    c: Equal(g8,g7)
    c: Radius(g7) = 1.5
    c: Angle(g4,g5) = 0.261799
    c: Angle(g6,g4) = 0.261799
FEATURE [PartDesign::Pad] Pad007
  Direction = (0,0,1)
  Length = 5
  Length2 = 10
  Profile = -> Sketch014
  ReferenceAxis = -> Sketch014 [N_Axis]
  Reversed = true
  Suppressed = false
  Type = 0
FEATURE [Sketcher::SketchObject] Sketch015
  ArcFitTolerance = 1e-06
  AttachmentSupport = -> [XY_Plane004]
  FullyConstrained = true
  MakeInternals = false
  MapMode = 5
  sketch-geometry (2):
    g0: Circle CenterX=47 CenterY=-5e-16 CenterZ=0 NormalX=0 NormalY=0 NormalZ=1 AngleXU=0 Radius=5
    g1: LineSegment [constr] StartX=0 StartY=0 StartZ=0 EndX=47 EndY=-5e-16 EndZ=0
  constraints (5):
    c: Coincident(g1,g-1)
    c: Coincident(g1,g0)
    c: Distance(g1) = 47
    c: Angle(g-1,g1) = 0
    c: Radius(g0) = 5
FEATURE [PartDesign::Pad] Pad008
  BaseFeature = -> Pad007
  Direction = (0,0,1)
  Length = 33
  Length2 = 10
  Profile = -> Sketch015
  ReferenceAxis = -> Sketch015 [N_Axis]
  Reversed = true
  Suppressed = false
  Type = 0
FEATURE [Sketcher::SketchObject] Sketch016
  ArcFitTolerance = 1e-06
  AttachmentSupport = -> [XZ_Plane004]
  FullyConstrained = true
  MakeInternals = false
  MapMode = 5
  Placement = pos=(0,0,0) rot=(1,0,0;1.5708rad)
  sketch-geometry (5):
    g0: LineSegment StartX=47 StartY=-5 StartZ=0 EndX=47 EndY=-33 EndZ=0
    g1: LineSegment StartX=47 StartY=-33 StartZ=0 EndX=72 EndY=-33 EndZ=0
    g2: LineSegment StartX=72 StartY=-33 StartZ=0 EndX=72 EndY=-25 EndZ=0
    g3: LineSegment StartX=52 StartY=-5 StartZ=0 EndX=47 EndY=-5 EndZ=0
    g4: ArcOfCircle CenterX=72 CenterY=-5 CenterZ=0 NormalX=0 NormalY=0 NormalZ=1 AngleXU=0 Radius=20 StartAngle=3.14159 EndAngle=4.71239
  constraints (16):
    c: Coincident(g0,g1)
    c: Coincident(g1,g2)
    c: Coincident(g3,g0)
    c: Vertical(g0)
    c: Vertical(g2)
    c: Horizontal(g1)
    c: Horizontal(g3)
    c: Coincident(g4,g3)
    c: Coincident(g4,g2)
    c: DistanceX(g0) = 47
    c: DistanceY(g0) = -5
    c: DistanceY(g0,g-1) = 33
    c: DistanceX(g3,g3) = 5
    c: DistanceX(g1,g1) = 25
    c: DistanceX(g4,g2) = 0
    c: DistanceY(g3,g4) = 0
FEATURE [PartDesign::Pad] Pad009
  BaseFeature = -> Pad008
  Direction = (0,-1,2e-16)
  Length = 10
  Length2 = 10
  Midplane = true
  Profile = -> Sketch016
  ReferenceAxis = -> Sketch016 [N_Axis]
  Suppressed = false
  Type = 0
FEATURE [Sketcher::SketchObject] Sketch017
  ArcFitTolerance = 1e-06
  AttachmentOffset = pos=(0,0,-33) rot=(0,0,1;0rad)
  AttachmentSupport = -> [XY_Plane004]
  FullyConstrained = true
  MakeInternals = false
  MapMode = 5
  Placement = pos=(0,0,-33) rot=(0,0,1;0rad)
  sketch-geometry (2):
    g0: ArcOfCircle CenterX=72 CenterY=0 CenterZ=0 NormalX=0 NormalY=0 NormalZ=1 AngleXU=0 Radius=5 StartAngle=4.71239 EndAngle=7.85398
    g1: LineSegment StartX=72 StartY=5 StartZ=0 EndX=72 EndY=-5 EndZ=0
  constraints (7):
    c: PointOnObject(g0,g-1)
    c: Coincident(g1,g0)
    c: Coincident(g1,g0)
    c: Vertical(g1)
    c: Radius(g0) = 5
    c: DistanceX(g0,g0) = 0
    c: DistanceX(g-1,g0) = 72
FEATURE [PartDesign::Pad] Pad010
  BaseFeature = -> Pad009
  Direction = (0,0,1)
  Length = 8
  Length2 = 10
  Profile = -> Sketch017
  ReferenceAxis = -> Sketch017 [N_Axis]
  Suppressed = false
  Type = 0
FEATURE [PartDesign::Body] Body004  label="Leg1"
  AllowCompound = false
  Group = -> [Sketch014,Pad007,Sketch015,Pad008,Sketch016,Pad009,Sketch017,Pad010]
  Origin = -> Origin004
  Placement = pos=(0,0,23) rot=(0,0,1;0.785398rad)
  Tip = -> Pad010
COMPONENT P5 — same part as P4; its construction recipe is shown at P4.
COMPONENT P6 — same part as P4; its construction recipe is shown at P4.
PROVENANCE & LICENSES
A FreeCAD (.FCStd) document from a public repository crawl; recipes are the document's own serialized feature recipes (and, for linked parts, companion documents' recipes).
License: as declared in the source repository (recorded in the dataset sidecar).
